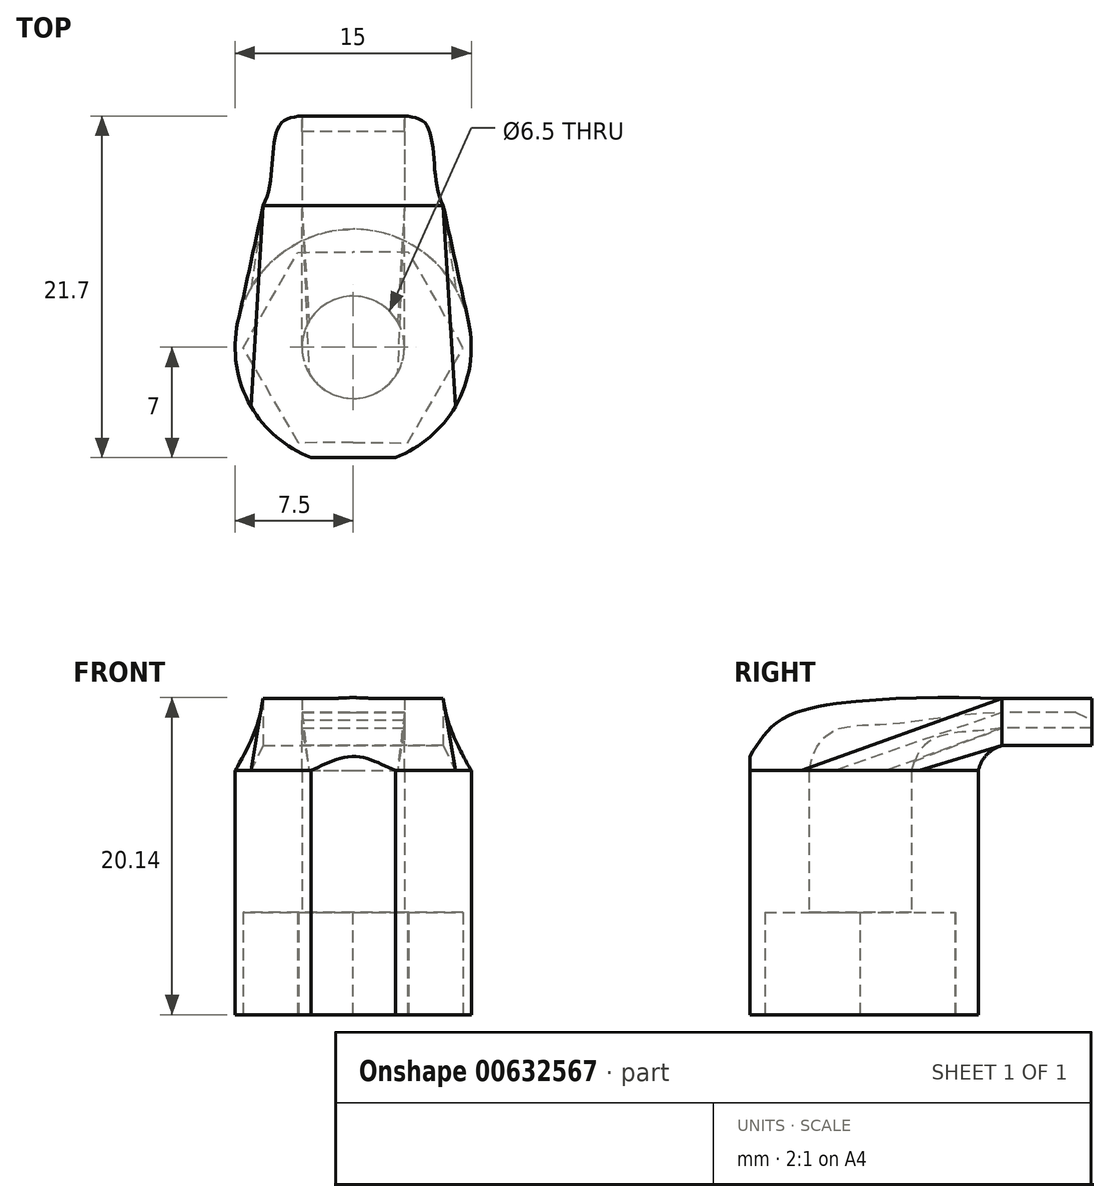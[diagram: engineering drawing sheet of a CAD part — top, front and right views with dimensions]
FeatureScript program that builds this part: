
annotation { "Feature Type Name" : "Feature", "Feature Type Description" : "" }
export const myFeature = defineFeature(function(context is Context, id is Id, definition is map)
    precondition{}
    {
        {
            var Q0;
            Q0=qCreatedBy(makeId("Top.planeOp"),FACE);
            var sketch = newSketch(context, id + "F0", { "sketchPlane" : qUnion([Q0])});
            skCircle(sketch, "E0.cCircle", {"center": v(0, 0) * mm, "radius": 6.05 * mm, "construction": true});
            skLineSegment(sketch, "E0.0", {"start": v(3.46, 6.07) * mm, "end": v(6.99, 0.04) * mm});
            skLineSegment(sketch, "E0.1", {"start": v(6.99, 0.04) * mm, "end": v(3.53, -6.03) * mm});
            skLineSegment(sketch, "E0.2", {"start": v(3.53, -6.03) * mm, "end": v(-3.46, -6.07) * mm});
            skLineSegment(sketch, "E0.3", {"start": v(-3.46, -6.07) * mm, "end": v(-6.99, -0.04) * mm});
            skLineSegment(sketch, "E0.4", {"start": v(-6.99, -0.04) * mm, "end": v(-3.53, 6.03) * mm});
            skLineSegment(sketch, "E0.5", {"start": v(-3.53, 6.03) * mm, "end": v(3.46, 6.07) * mm});
            skPoint(sketch, "E0.0.midPoint", {"position": v(5.22, 3.05) * mm});
            skCircle(sketch, "E1", {"center": v(0, 0) * mm, "radius": 7.5 * mm});
            skSolve(sketch);
        }
        {
            var Q0;
            Q0=makeQuery(id+"F0.imprint","IMPRINT",FACE,{"disambiguationData":[TD([[makeQuery(id+"F0.imprint","IMPRINT",EDGE,{"derivedFrom":sQuery(id+"F0.wireOp",EDGE,"E0.0")}),1.0]])]});
            extrude(context, id + "F1", {"entities" : qUnion([Q0]), "depth" : 6.5 * mm, "offsetDistance" : 25 * mm});
        }
        {
            var Q0;
            Q0=makeQuery(id+"F1.opExtrude","CAP_FACE",FACE,{"disambiguationData":[OSD([sQuery(id+"F0.wireOp",EDGE,"E0.0"),sQuery(id+"F0.wireOp",EDGE,"E0.1"),sQuery(id+"F0.wireOp",EDGE,"E0.2"),sQuery(id+"F0.wireOp",EDGE,"E0.3"),sQuery(id+"F0.wireOp",EDGE,"E0.4"),sQuery(id+"F0.wireOp",EDGE,"E0.5"),sQuery(id+"F0.wireOp",EDGE,"E1")])],"isStart":false});
            cPlane(context, id + "F2", {"entities" : qUnion([Q0]), "cplaneType" : CPlaneType.OFFSET, "offset" : 0 * mm, "width" : 150 * mm, "height" : 150 * mm});
        }
        {
            var Q0;
            Q0=qCreatedBy(id+"F2.planeOp",FACE);
            var sketch = newSketch(context, id + "F3", { "sketchPlane" : qUnion([Q0])});
            skCircle(sketch, "E2", {"center": v(0, 0) * mm, "radius": 7.5 * mm});
            skCircle(sketch, "E3", {"center": v(0, 0) * mm, "radius": 3.25 * mm});
            skSolve(sketch);
        }
        {
            var Q0;
            Q0=makeQuery(id+"F0.imprint","IMPRINT",FACE,{"disambiguationData":[TD([[makeQuery(id+"F0.imprint","IMPRINT",EDGE,{"derivedFrom":sQuery(id+"F0.wireOp",EDGE,"E0.0")}),1.0]])]});
            cPlane(context, id + "F4", {"entities" : qUnion([Q0]), "cplaneType" : CPlaneType.OFFSET, "offset" : 0 * mm, "width" : 150 * mm, "height" : 150 * mm});
        }
        {
            var Q0;
            Q0=qCreatedBy(id+"F4.planeOp",FACE);
            var sketch = newSketch(context, id + "F5", { "sketchPlane" : qUnion([Q0])});
            skLineSegment(sketch, "E4", {"start": v(0, 0) * mm, "end": v(0, -7) * mm, "construction": true});
            skLineSegment(sketch, "E5", {"start": v(0, -7) * mm, "end": v(5.15, -7) * mm});
            skLineSegment(sketch, "E6", {"start": v(5.15, -7) * mm, "end": v(5.15, -7.55) * mm});
            skLineSegment(sketch, "E7", {"start": v(5.15, -7.55) * mm, "end": v(-6.58, -7.55) * mm});
            skLineSegment(sketch, "E8", {"start": v(-6.58, -7.55) * mm, "end": v(-6.58, -7) * mm});
            skLineSegment(sketch, "E9", {"start": v(-6.58, -7) * mm, "end": v(0, -7) * mm});
            skSolve(sketch);
        }
        {
            var Q0;
            Q0=qCreatedBy(makeId("Top.planeOp"),FACE);
            var sketch = newSketch(context, id + "F6", { "sketchPlane" : qUnion([Q0])});
            skLineSegment(sketch, "E10.bottom", {"start": v(0, -8.32) * mm, "end": v(19.03, -8.32) * mm});
            skLineSegment(sketch, "E10.top", {"start": v(0, 21.36) * mm, "end": v(19.03, 21.36) * mm});
            skLineSegment(sketch, "E10.left", {"start": v(0, -8.32) * mm, "end": v(0, 21.36) * mm});
            skLineSegment(sketch, "E10.right", {"start": v(19.03, -8.32) * mm, "end": v(19.03, 21.36) * mm});
            skSolve(sketch);
        }
        {
            var Q0;
            Q0=makeQuery(id+"F6.imprint","IMPRINT",FACE,{"disambiguationData":[TD([[makeQuery(id+"F6.imprint","IMPRINT",EDGE,{"derivedFrom":sQuery(id+"F6.wireOp",EDGE,"E10.bottom")}),1.0]])]});
            extrude(context, id + "F7", {"entities" : qUnion([Q0]), "operationType" : NewBodyOperationType.REMOVE, "depth" : 25 * mm, "offsetDistance" : 25 * mm});
        }
        {
            var Q0;
            Q0=makeQuery(id+"F1.opExtrude","SWEPT_BODY",BODY,{"disambiguationData":[OSD([sQuery(id+"F0.wireOp",EDGE,"E0.0"),sQuery(id+"F0.wireOp",EDGE,"E0.1"),sQuery(id+"F0.wireOp",EDGE,"E0.2"),sQuery(id+"F0.wireOp",EDGE,"E0.3"),sQuery(id+"F0.wireOp",EDGE,"E0.4"),sQuery(id+"F0.wireOp",EDGE,"E0.5"),sQuery(id+"F0.wireOp",EDGE,"E1")])]});
            var Q1;
            {var subQ3=sQuery(id+"F0.wireOp",EDGE,"E0.5");Q1=makeQuery(id+"F7.boolean.opBoolean","COPY",FACE,{"disambiguationData":[TD([makeQuery(id+"F1.opExtrude","SWEPT_FACE",FACE,{"disambiguationData":[OSD([subQ3])]})])],"derivedFrom":makeQuery(id+"F7.opExtrude","SWEPT_FACE",FACE,{"disambiguationData":[OSD([sQuery(id+"F6.wireOp",EDGE,"E10.left")])]})});}
            mirror(context, id + "F8", {"operationType" : NewBodyOperationType.ADD, "entities" : qUnion([Q0]), "mirrorPlane" : qUnion([Q1])});
        }
        {
            var Q0;
            Q0=qCreatedBy(makeId("Front.planeOp"),FACE);
            var sketch = newSketch(context, id + "F9", { "sketchPlane" : qUnion([Q0])});
            skLineSegment(sketch, "E11", {"start": v(0, 0) * mm, "end": v(0, 6.5) * mm, "construction": true});
            skLineSegment(sketch, "E12", {"start": v(0, 6.5) * mm, "end": v(0, 15.5) * mm});
            skLineSegment(sketch, "E13", {"start": v(0, 6.5) * mm, "end": v(3.25, 6.5) * mm});
            skLineSegment(sketch, "E14", {"start": v(3.25, 6.5) * mm, "end": v(7.5, 6.5) * mm});
            skLineSegment(sketch, "E15", {"start": v(7.5, 6.5) * mm, "end": v(7.5, 15.5) * mm});
            skLineSegment(sketch, "E16", {"start": v(3.25, 6.5) * mm, "end": v(3.25, 15.5) * mm});
            skLineSegment(sketch, "E17", {"start": v(0, 15.5) * mm, "end": v(7.5, 15.5) * mm});
            skLineSegment(sketch, "E18.bottom", {"start": v(0, 15.5) * mm, "end": v(3.25, 15.5) * mm});
            skLineSegment(sketch, "E18.top", {"start": v(0, 15.35) * mm, "end": v(3.25, 15.35) * mm});
            skLineSegment(sketch, "E18.left", {"start": v(0, 15.5) * mm, "end": v(0, 15.35) * mm});
            skLineSegment(sketch, "E18.right", {"start": v(3.25, 15.5) * mm, "end": v(3.25, 15.35) * mm});
            skSolve(sketch);
        }
        {
            var Q0;
            {var subQ4=sQuery(id+"F9.wireOp",EDGE,"E14");Q0=makeQuery(id+"F9.imprint","IMPRINT",FACE,{"disambiguationData":[TD([[makeQuery(id+"F9.imprint","IMPRINT",EDGE,{"derivedFrom":subQ4}),1.0]])]});}
            var Q1;
            Q1=sQuery(id+"F9.wireOp",EDGE,"E12");
            revolve(context, id + "F10", {"operationType" : NewBodyOperationType.ADD, "surfaceOperationType" : NewSurfaceOperationType.NEW, "entities" : qUnion([Q0]), "axis" : qUnion([Q1]), "revolveType" : RevolveType.FULL});
        }
        {
            var Q0;
            Q0=makeQuery(id+"F10.opRevolve","SWEPT_FACE",FACE,{"disambiguationData":[OSD([sQuery(id+"F9.wireOp",EDGE,"E17")])]});
            cPlane(context, id + "F11", {"entities" : qUnion([Q0]), "cplaneType" : CPlaneType.OFFSET, "offset" : 1.6 * mm, "width" : 150 * mm, "height" : 150 * mm});
        }
        {
            var Q0;
            Q0=qCreatedBy(id+"F11.planeOp",FACE);
            var sketch = newSketch(context, id + "F12", { "sketchPlane" : qUnion([Q0])});
            skPoint(sketch, "E19", {"position": v(-3.25, 0) * mm});
            skPoint(sketch, "E20", {"position": v(3.25, 0) * mm});
            skPoint(sketch, "E21", {"position": v(0, 7.5) * mm});
            skLineSegment(sketch, "E22", {"start": v(3.25, 0) * mm, "end": v(3.25, 7.5) * mm, "construction": true});
            skLineSegment(sketch, "E23", {"start": v(0, 7.5) * mm, "end": v(3.25, 7.5) * mm});
            skLineSegment(sketch, "E24", {"start": v(3.25, 14.7) * mm, "end": v(3.25, 7.5) * mm});
            skLineSegment(sketch, "E25", {"start": v(3.25, 14.7) * mm, "end": v(0, 14.7) * mm});
            skLineSegment(sketch, "E26", {"start": v(0, 14.7) * mm, "end": v(0, 7.5) * mm});
            skLineSegment(sketch, "E27.MirrorCS", {"start": v(-3.25, 14.7) * mm, "end": v(-3.25, 7.5) * mm});
            skLineSegment(sketch, "E28.MirrorCS", {"start": v(-3.25, 14.7) * mm, "end": v(0, 14.7) * mm});
            skLineSegment(sketch, "E29.MirrorCS", {"start": v(0, 7.5) * mm, "end": v(-3.25, 7.5) * mm});
            skPoint(sketch, "E30", {"position": v(0, 9) * mm});
            skLineSegment(sketch, "E31", {"start": v(0, 9) * mm, "end": v(3.25, 9) * mm});
            skLineSegment(sketch, "E32", {"start": v(0, 9) * mm, "end": v(-3.25, 9) * mm});
            skLineSegment(sketch, "E33", {"start": v(-3.25, 7.5) * mm, "end": v(-6.85, 7.5) * mm});
            skFitSpline(sketch, "E34", {"points": [v(-6.85, 7.5) * mm, v(-5.54, 9.4) * mm, v(-5.09, 12.4) * mm, v(-4.52, 14.29) * mm, v(-3.25, 14.7) * mm], "startDerivative": vector(5.88, 6.52) * mm, "endDerivative": vector(7.26, 0.85) * mm});
            skFitSpline(sketch, "E35.MirrorCS", {"points": [v(6.85, 7.5) * mm, v(5.54, 9.4) * mm, v(5.09, 12.4) * mm, v(4.52, 14.29) * mm, v(3.25, 14.7) * mm], "startDerivative": vector(-5.88, 6.52) * mm, "endDerivative": vector(-7.26, 0.85) * mm});
            skLineSegment(sketch, "E36.MirrorCS", {"start": v(3.25, 7.5) * mm, "end": v(6.85, 7.5) * mm});
            skLineSegment(sketch, "E37", {"start": v(-3.25, 9) * mm, "end": v(-5.72, 9) * mm});
            skLineSegment(sketch, "E38", {"start": v(-5.72, 9) * mm, "end": v(3.25, 9) * mm});
            skLineSegment(sketch, "E39", {"start": v(3.25, 9) * mm, "end": v(5.72, 9) * mm});
            skSolve(sketch);
        }
        {
            var Q0;
            {var subQ3=sQuery(id+"F12.wireOp",EDGE,"E39");Q0=makeQuery(id+"F12.imprint","IMPRINT",FACE,{"disambiguationData":[TD([[makeQuery(id+"F12.imprint","IMPRINT",EDGE,{"derivedFrom":subQ3}),1.0]])]});}
            var Q1;
            {var subQ0=sQuery(id+"F12.wireOp",EDGE,"E25");Q1=makeQuery(id+"F12.imprint","IMPRINT",FACE,{"disambiguationData":[TD([[makeQuery(id+"F12.imprint","IMPRINT",EDGE,{"derivedFrom":subQ0}),1.0]])]});}
            var Q2;
            {var subQ0=sQuery(id+"F12.wireOp",EDGE,"E28.MirrorCS");Q2=makeQuery(id+"F12.imprint","IMPRINT",FACE,{"disambiguationData":[TD([[makeQuery(id+"F12.imprint","IMPRINT",EDGE,{"derivedFrom":subQ0}),-1.0]])]});}
            var Q3;
            {var subQ3=sQuery(id+"F12.wireOp",EDGE,"E37");Q3=makeQuery(id+"F12.imprint","IMPRINT",FACE,{"disambiguationData":[TD([[makeQuery(id+"F12.imprint","IMPRINT",EDGE,{"derivedFrom":subQ3}),-1.0]])]});}
            extrude(context, id + "F13", {"entities" : qUnion([Q0, Q1, Q2, Q3]), "depth" : 3 * mm, "offsetDistance" : 25 * mm});
        }
        {
            var Q0;
            Q0=qCreatedBy(makeId("Right.planeOp"),FACE);
            var sketch = newSketch(context, id + "F14", { "sketchPlane" : qUnion([Q0])});
            skPoint(sketch, "E40", {"position": v(9, 17.1) * mm});
            skPoint(sketch, "E41", {"position": v(0, 17.1) * mm});
            skPoint(sketch, "E42", {"position": v(7.5, 17.1) * mm});
            skPoint(sketch, "E43", {"position": v(0, 15.5) * mm});
            skPoint(sketch, "E44", {"position": v(-7.5, 17.1) * mm});
            skPoint(sketch, "E45", {"position": v(-7.5, 15.5) * mm});
            skPoint(sketch, "E46", {"position": v(7.5, 15.5) * mm});
            skArc(sketch, "E47", {"start": v(9, 17.1) * mm, "mid": v(8.02, 16.51) * mm, "end": v(7.5, 15.5) * mm});
            skPoint(sketch, "E48", {"position": v(9, 20.1) * mm});
            skPoint(sketch, "E49", {"position": v(3.25, 15.5) * mm});
            skPoint(sketch, "E50", {"position": v(-3.25, 15.5) * mm});
            skPoint(sketch, "E51", {"position": v(9, 18.2) * mm});
            skPoint(sketch, "E52", {"position": v(9, 19.2) * mm});
            skFitSpline(sketch, "E53", {"points": [v(-7.5, 15.5) * mm, v(-5.77, 18.13) * mm, v(-3.3, 19.42) * mm, v(2.94, 20.1) * mm, v(9, 20.1) * mm], "startDerivative": vector(7.52, 13.91) * mm, "endDerivative": vector(20, -0.39) * mm});
            skFitSpline(sketch, "E54", {"points": [v(-3.25, 15.5) * mm, v(-2.88, 16.77) * mm, v(-1.66, 18.05) * mm, v(2.1, 18.5) * mm, v(9, 19.2) * mm], "startDerivative": vector(1.59, 7.77) * mm, "endDerivative": vector(19.44, -0.03) * mm});
            skFitSpline(sketch, "E55", {"points": [v(3.25, 15.5) * mm, v(3.9, 16.91) * mm, v(5.28, 17.75) * mm, v(7.67, 18.05) * mm, v(9, 18.2) * mm], "startDerivative": vector(2.14, 6.43) * mm, "endDerivative": vector(5.43, 0.75) * mm});
            skSolve(sketch);
        }
        {
            var Q0;
            Q0=makeQuery(id+"F13.opExtrude","SWEPT_FACE",FACE,{"disambiguationData":[OSD([sQuery(id+"F12.wireOp",EDGE,"E31"),sQuery(id+"F12.wireOp",EDGE,"E32"),sQuery(id+"F12.wireOp",EDGE,"E37"),sQuery(id+"F12.wireOp",EDGE,"E39")])]});
            var sketch = newSketch(context, id + "F15", { "sketchPlane" : qUnion([Q0])});
            skPoint(sketch, "E56", {"position": v(0, 17.1) * mm});
            skPoint(sketch, "E57", {"position": v(0, 18.2) * mm});
            skPoint(sketch, "E58", {"position": v(0, 18.1) * mm});
            skLineSegment(sketch, "E59.bottom", {"start": v(0, 18.2) * mm, "end": v(3.25, 18.2) * mm});
            skLineSegment(sketch, "E59.top", {"start": v(0, 19.2) * mm, "end": v(3.25, 19.2) * mm});
            skLineSegment(sketch, "E59.right", {"start": v(3.25, 18.2) * mm, "end": v(3.25, 19.2) * mm});
            skLineSegment(sketch, "E60.bottom", {"start": v(0, 18.2) * mm, "end": v(-3.25, 18.2) * mm});
            skLineSegment(sketch, "E60.top", {"start": v(0, 19.2) * mm, "end": v(-3.25, 19.2) * mm});
            skLineSegment(sketch, "E60.right", {"start": v(-3.25, 18.2) * mm, "end": v(-3.25, 19.2) * mm});
            skSolve(sketch);
        }
        {
            var Q0;
            {var subQ3=sQuery(id+"F9.wireOp",EDGE,"E18.top");Q0=makeQuery(id+"F9.imprint","IMPRINT",FACE,{"disambiguationData":[TD([[makeQuery(id+"F9.imprint","IMPRINT",EDGE,{"derivedFrom":subQ3}),1.0]])]});}
            var Q1;
            Q1=sQuery(id+"F9.wireOp",EDGE,"E12");
            revolve(context, id + "F16", {"operationType" : NewBodyOperationType.ADD, "surfaceOperationType" : NewSurfaceOperationType.NEW, "entities" : qUnion([Q0]), "axis" : qUnion([Q1]), "revolveType" : RevolveType.FULL});
        }
        {
            var Q0;
            {var subQ0=sQuery(id+"F9.wireOp",EDGE,"E17");Q0=makeQuery(id+"F16.boolean.opBoolean","MERGE",FACE,{"derivedFrom":[makeQuery(id+"F10.opRevolve","SWEPT_FACE",FACE,{"disambiguationData":[OSD([subQ0])]}),makeQuery(id+"F16.opRevolve","SWEPT_FACE",FACE,{"disambiguationData":[OSD([subQ0])]})]});}
            var sketch = newSketch(context, id + "F17", { "sketchPlane" : qUnion([Q0])});
            skCircle(sketch, "E61", {"center": v(0, 0) * mm, "radius": 3.25 * mm});
            skSolve(sketch);
        }
        {
            var Q1;
            Q1=makeQuery(id+"F13.opExtrude","SWEPT_FACE",FACE,{"disambiguationData":[OSD([sQuery(id+"F12.wireOp",EDGE,"E31"),sQuery(id+"F12.wireOp",EDGE,"E32"),sQuery(id+"F12.wireOp",EDGE,"E37"),sQuery(id+"F12.wireOp",EDGE,"E39")])]});
            var Q2;
            {var subQ0=sQuery(id+"F9.wireOp",EDGE,"E17");Q2=makeQuery(id+"F16.boolean.opBoolean","MERGE",FACE,{"derivedFrom":[makeQuery(id+"F10.opRevolve","SWEPT_FACE",FACE,{"disambiguationData":[OSD([subQ0])]}),makeQuery(id+"F16.opRevolve","SWEPT_FACE",FACE,{"disambiguationData":[OSD([subQ0])]})]});}
            var Q3;
            Q3=sQuery(id+"F14.wireOp",EDGE,"E53");
            var Q4;
            Q4=sQuery(id+"F14.wireOp",EDGE,"E47");
            loft(context, id + "F18", {"operationType" : NewBodyOperationType.ADD, "addGuides" : true, "sheetProfilesArray" : [{ "sheetProfileEntities" : qUnion([Q1]) }, { "sheetProfileEntities" : qUnion([Q2]) }], "guidesArray" : [{ "guideEntities" : qUnion([Q3]), "guideDerivativeType" : LoftGuideDerivativeType.DEFAULT, "guideDerivativeMagnitude" : 1 }, { "guideEntities" : qUnion([Q4]), "guideDerivativeType" : LoftGuideDerivativeType.DEFAULT, "guideDerivativeMagnitude" : 1 }]});
        }
        {
            var Q0;
            Q0=makeQuery(id+"F15.imprint","IMPRINT",FACE,{"disambiguationData":[TD([[makeQuery(id+"F15.imprint","IMPRINT",EDGE,{"derivedFrom":sQuery(id+"F15.wireOp",EDGE,"E59.bottom")}),1.0]])]});
            extrude(context, id + "F19", {"entities" : qUnion([Q0]), "operationType" : NewBodyOperationType.REMOVE, "oppositeDirection" : true, "depth" : .1 * mm, "offsetDistance" : 25 * mm});
        }
        {
            var Q1;
            Q1=makeQuery(id+"F15.imprint","IMPRINT",FACE,{"disambiguationData":[TD([[makeQuery(id+"F15.imprint","IMPRINT",EDGE,{"derivedFrom":sQuery(id+"F15.wireOp",EDGE,"E59.bottom")}),1.0]])]});
            var Q2;
            Q2=makeQuery(id+"F17.imprint","IMPRINT",FACE,{"disambiguationData":[TD([[makeQuery(id+"F17.imprint","IMPRINT",EDGE,{"derivedFrom":sQuery(id+"F17.wireOp",EDGE,"E61")}),1.0]])]});
            var Q3;
            Q3=sQuery(id+"F14.wireOp",EDGE,"E54");
            var Q4;
            Q4=sQuery(id+"F14.wireOp",EDGE,"E55");
            loft(context, id + "F20", {"operationType" : NewBodyOperationType.REMOVE, "addGuides" : true, "sheetProfilesArray" : [{ "sheetProfileEntities" : qUnion([Q1]) }, { "sheetProfileEntities" : qUnion([Q2]) }], "guidesArray" : [{ "guideEntities" : qUnion([Q3]), "guideDerivativeType" : LoftGuideDerivativeType.DEFAULT, "guideDerivativeMagnitude" : 1 }, { "guideEntities" : qUnion([Q4]), "guideDerivativeType" : LoftGuideDerivativeType.DEFAULT, "guideDerivativeMagnitude" : 1 }]});
        }
        {
            var Q0;
            Q0 = qSketchRegion(id + "F17", true);
            extrude(context, id + "F21", {"entities" : qUnion([Q0]), "operationType" : NewBodyOperationType.REMOVE, "oppositeDirection" : true, "depth" : 25 * mm, "offsetDistance" : 25 * mm});
        }
        {
            var Q0;
            Q0=makeQuery(id+"F15.imprint","IMPRINT",FACE,{"disambiguationData":[TD([[makeQuery(id+"F15.imprint","IMPRINT",EDGE,{"derivedFrom":sQuery(id+"F15.wireOp",EDGE,"E59.bottom")}),1.0]])]});
            extrude(context, id + "F22", {"entities" : qUnion([Q0]), "operationType" : NewBodyOperationType.REMOVE, "oppositeDirection" : true, "depth" : 25 * mm, "offsetDistance" : 25 * mm});
        }
        {
            var Q0;
            Q0 = qSketchRegion(id + "F5", true);
            extrude(context, id + "F23", {"entities" : qUnion([Q0]), "operationType" : NewBodyOperationType.REMOVE, "depth" : 25 * mm, "offsetDistance" : 25 * mm});
        }
        {
            var Q0;
            {var subQ0=sQuery(id+"F15.wireOp",EDGE,"E60.right");Q0=makeQuery(id+"F22.boolean.opBoolean","MERGE",FACE,{"derivedFrom":[makeQuery(id+"F19.boolean.opBoolean","COPY",FACE,{"derivedFrom":makeQuery(id+"F19.opExtrude","SWEPT_FACE",FACE,{"disambiguationData":[OSD([subQ0])]})}),makeQuery(id+"F22.opExtrude","SWEPT_FACE",FACE,{"disambiguationData":[OSD([subQ0])]})]});}
            var sketch = newSketch(context, id + "F24", { "sketchPlane" : qUnion([Q0])});
            skPoint(sketch, "E62", {"position": v(14.7, 19.2) * mm});
            skPoint(sketch, "E63", {"position": v(14.7, 18.7) * mm});
            skPoint(sketch, "E64", {"position": v(13.7, 19.2) * mm});
            skLineSegment(sketch, "E65", {"start": v(13.7, 19.2) * mm, "end": v(14.7, 19.2) * mm});
            skLineSegment(sketch, "E66", {"start": v(14.7, 18.7) * mm, "end": v(14.7, 19.2) * mm});
            skLineSegment(sketch, "E67", {"start": v(13.7, 19.2) * mm, "end": v(14.7, 18.7) * mm});
            skSolve(sketch);
        }
        {
            var Q0;
            Q0=makeQuery(id+"F24.imprint","IMPRINT",FACE,{"disambiguationData":[TD([[makeQuery(id+"F24.imprint","IMPRINT",EDGE,{"derivedFrom":sQuery(id+"F24.wireOp",EDGE,"E65")}),1.0]])]});
            extrude(context, id + "F25", {"entities" : qUnion([Q0]), "operationType" : NewBodyOperationType.ADD, "depth" : 6.5 * mm, "offsetDistance" : 25 * mm});
        }
    });
